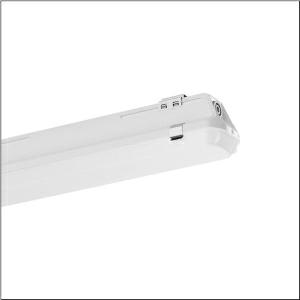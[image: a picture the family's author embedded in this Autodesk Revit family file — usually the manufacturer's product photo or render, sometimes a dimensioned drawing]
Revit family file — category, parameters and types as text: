
# Revit family: monsun_r__21_51fb107p480b_58b6
name_source: partatom
category: Lighting Fixtures
units: mm (PartAtom-declared; Revit-internal decimal feet)

## family parameters
Cut with Voids When Loaded = No
Host = Face
Light Source = No
Part Type = Normal
Room Calculation Point = No
Round Connector Dimension = Use Diameter
Shared = No

## types (1)
- Monsun® 21 (1 x LED, 8070 lm, 52.8 W, 4000K)
    Apparent Load = 53 VA
    CIE Flux Codes = 47 77 93 94 100
    Color Rendering = 80
    Color Temperature = 4000K
    Default Elevation = 1800 mm
    Description = Monsun® 21, damp-proof luminaire, chain hanger, primary optical cover: enclosure, of PMMA, light emission: direct distribution, primary light characteristic: symmetric, installation type: suspended mounting, surface-mounted, horizontal mounting, vertical mounting, LED, rated luminous flux: 8.070lm, luminous efficacy: 153lm/W, light colour: 840, colour temperature: 4000K, control gear: ECG, with terminal, 3-pole, max. 2.5mm², mains connection: 220..240V, AC, 50/60Hz, rated input power: 53W, housing, of glass-fibre reinforced polyester, uncoated, bright grey, incl. chain hanger, length: 1.590mm, width: 90mm, height: 88mm, clip for enclosure, of stainless steel (V2A), ceiling mounting element, of stainless steel (V2A), chain hanger, of stainless steel (V2A), protection rating (complete): IP66, insulation class (complete): insulation class I (protective earthing), certification: CE, ENEC, VDE, UKCA, protection symbol: D, impact resistance: IK04, permissible operating ambient temperature: -25..+35°C, standard: EN 50419, EN 60598-2-1, corresponds to IFS (International Featured Standards) requirements for safety and quality in the food industry, for indoor or canopied outdoor use, no direct snow, no direct sun, no direct rain, contact your sales advisor before using the luminaires in applications with unclear chemical exposure, large temperature fluctuations or condensation-forming humidity, LABS conformity tested according to VDMA 24364:2018-05, packaging unit: 1 piece
    Height = 89 mm
    Lamp = 1 x LED
    Lamp Light Flux = 8070 lm
    Lamp Power = 52.8 W
    Lamp count = 1
    Length = 1590 mm
    Luminous efficacy = 153 lm/W
    Manufacturer = Siteco
    ModVariant = No
    Model = 51FB107P480B
    Mounting Place = Ceiling
    Mounting Type = Surface mounted
    Number of Poles = 1
    OnlyDefault = Yes
    Power Factor = 1
    Product Name = Monsun® 21
    Product group = damp-proof luminaire
    ProductGroupID = 300
    Protection Class = Protection class I
    Protection Degree = IP 66
    RLX_Detail_Level = 1
    RLX_Emergency_Light_Flux = 0 lm
    RLX_Emergency_Type = 0
    RLX_Emergency_Type_DB = No
    RlxData = <blob elided: 88313 chars, md5=490a4474>
    Socket = socket
    Standby Power = 0 W
    System Light Flux = 8070 lm
    System Power = 53 W
    Type Comments = Product without accessories
    Type Image = l_1006717.jpg
    URL = http://relux.com
    VarID = ---
    Voltage = 0 V
    Weight = 0.00 kg
    Width = 90 mm

## geometry (parser evidence)
native form markers: Blend x4, Sweep x14
no freeform markers — native parametric forms only
